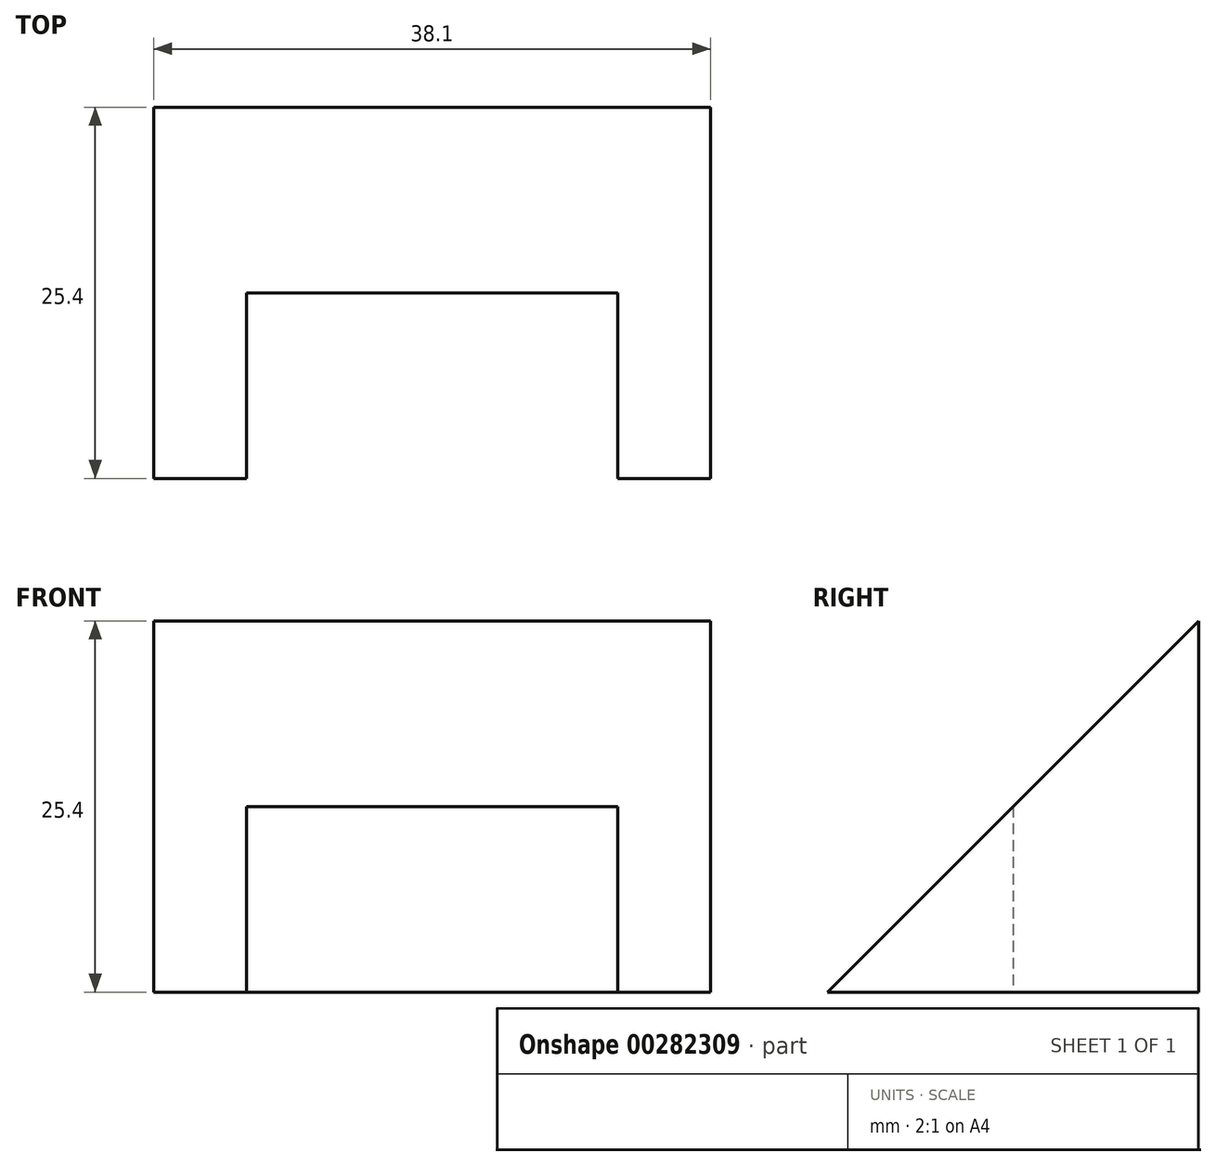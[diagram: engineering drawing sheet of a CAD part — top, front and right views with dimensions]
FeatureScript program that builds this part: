
annotation { "Feature Type Name" : "Feature", "Feature Type Description" : "" }
export const myFeature = defineFeature(function(context is Context, id is Id, definition is map)
    precondition{}
    {
        {
            var Q0;
            Q0=qCreatedBy(makeId("Right.planeOp"),FACE);
            var sketch = newSketch(context, id + "F0", { "sketchPlane" : qUnion([Q0])});
            skLineSegment(sketch, "E0", {"start": v(0, 0) * mm, "end": v(25.4, 25.4) * mm});
            skLineSegment(sketch, "E1", {"start": v(25.4, 25.4) * mm, "end": v(25.4, 0) * mm});
            skLineSegment(sketch, "E2", {"start": v(25.4, 0) * mm, "end": v(0, 0) * mm});
            skSolve(sketch);
        }
        {
            var Q0;
            Q0 = qSketchRegion(id + "F0", true);
            extrude(context, id + "F1", {"entities" : qUnion([Q0]), "depth" : 6.35 * mm});
        }
        {
            var Q0;
            Q0=makeQuery(id+"F1.opExtrude","CAP_FACE",FACE,{"disambiguationData":[OSD([sQuery(id+"F0.wireOp",EDGE,"E0"),sQuery(id+"F0.wireOp",EDGE,"E1"),sQuery(id+"F0.wireOp",EDGE,"E2")])],"isStart":false});
            var sketch = newSketch(context, id + "F2", { "sketchPlane" : qUnion([Q0])});
            skLineSegment(sketch, "E3", {"start": v(25.4, 25.4) * mm, "end": v(12.7, 12.7) * mm});
            skLineSegment(sketch, "E4", {"start": v(12.7, 12.7) * mm, "end": v(12.7, 0) * mm});
            skLineSegment(sketch, "E5", {"start": v(12.7, 0) * mm, "end": v(25.4, 0) * mm});
            skLineSegment(sketch, "E6", {"start": v(25.4, 0) * mm, "end": v(25.4, 25.4) * mm});
            skSolve(sketch);
        }
        {
            var Q0;
            Q0=makeQuery(id+"F2.imprint","IMPRINT",FACE,{"disambiguationData":[TD([[makeQuery(id+"F2.imprint","IMPRINT",EDGE,{"derivedFrom":sQuery(id+"F2.wireOp",EDGE,"E3")}),-1.0]])]});
            extrude(context, id + "F3", {"entities" : qUnion([Q0]), "operationType" : NewBodyOperationType.ADD, "depth" : 25.4 * mm});
        }
        {
            var Q0;
            Q0=makeQuery(id+"F3.opExtrude","CAP_FACE",FACE,{"disambiguationData":[OSD([sQuery(id+"F2.wireOp",EDGE,"E3"),sQuery(id+"F2.wireOp",EDGE,"E4"),sQuery(id+"F2.wireOp",EDGE,"E5"),sQuery(id+"F2.wireOp",EDGE,"E6")])],"isStart":false});
            var sketch = newSketch(context, id + "F4", { "sketchPlane" : qUnion([Q0])});
            skLineSegment(sketch, "E7", {"start": v(25.4, 25.4) * mm, "end": v(0, 0) * mm});
            skLineSegment(sketch, "E8", {"start": v(0, 0) * mm, "end": v(25.4, 0) * mm});
            skLineSegment(sketch, "E9", {"start": v(25.4, 0) * mm, "end": v(25.4, 25.4) * mm});
            skSolve(sketch);
        }
        {
            var Q0;
            Q0 = qSketchRegion(id + "F4", true);
            extrude(context, id + "F5", {"entities" : qUnion([Q0]), "operationType" : NewBodyOperationType.ADD, "depth" : 6.35 * mm});
        }
    });
